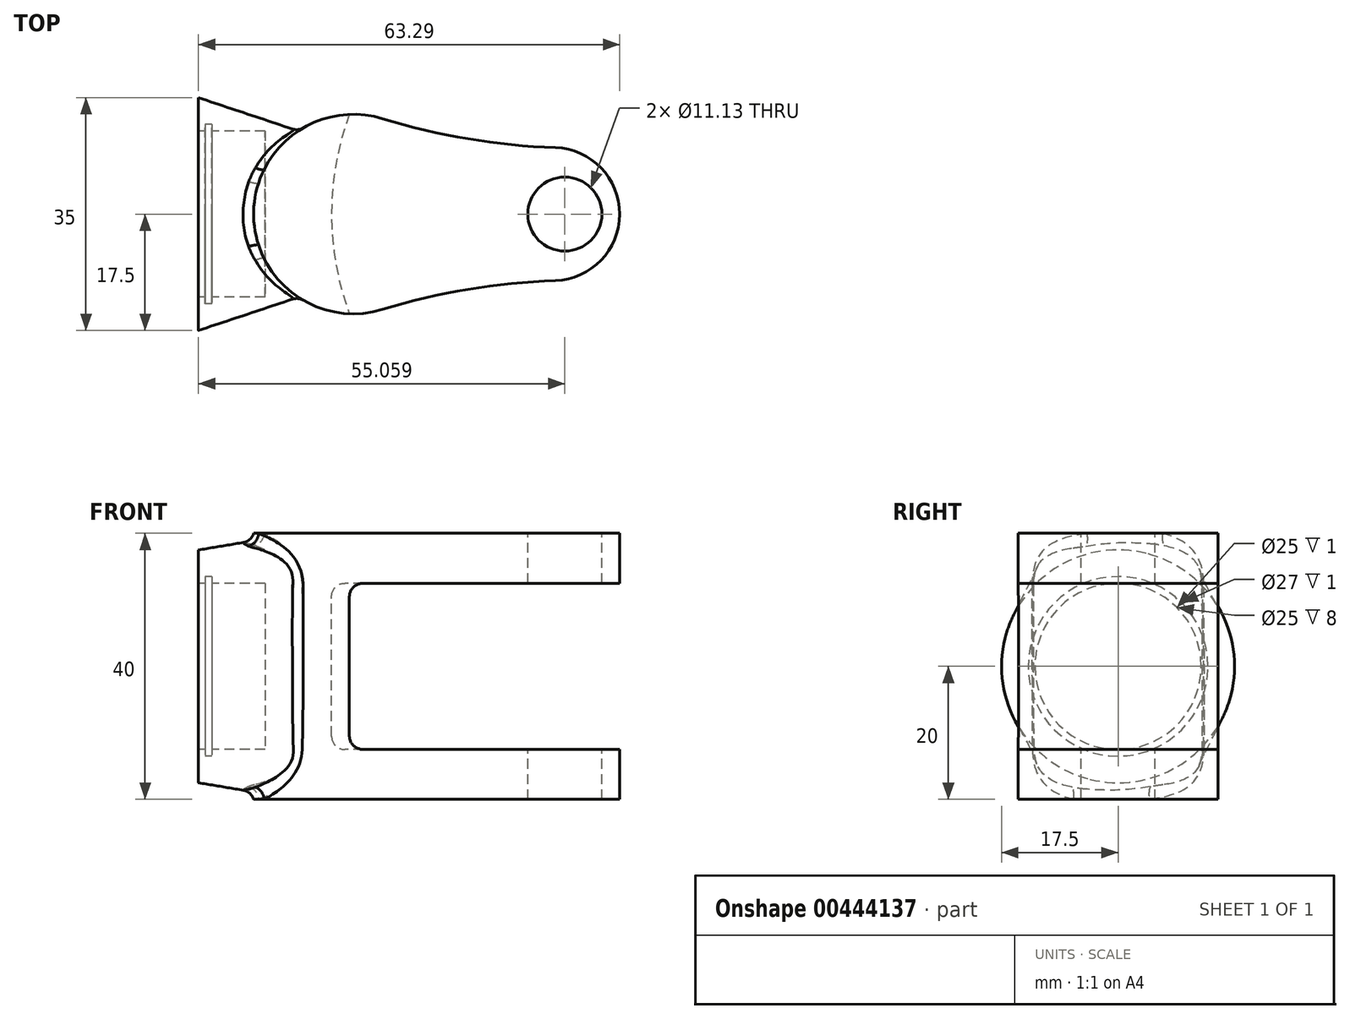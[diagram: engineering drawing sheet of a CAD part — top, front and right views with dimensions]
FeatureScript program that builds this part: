
annotation { "Feature Type Name" : "Feature", "Feature Type Description" : "" }
export const myFeature = defineFeature(function(context is Context, id is Id, definition is map)
    precondition{}
    {
        {
            var Q0;
            Q0=qCreatedBy(makeId("Right.planeOp"),FACE);
            var sketch = newSketch(context, id + "F0", { "sketchPlane" : qUnion([Q0])});
            skCircle(sketch, "E0", {"center": v(0, 0) * mm, "radius": 17.5 * mm});
            skSolve(sketch);
        }
        {
            var Q0;
            Q0=qCreatedBy(makeId("Right.planeOp"),FACE);
            cPlane(context, id + "F1", {"entities" : qUnion([Q0]), "cplaneType" : CPlaneType.OFFSET, "offset" : 15 * mm, "width" : 150 * mm, "height" : 150 * mm});
        }
        {
            var Q0;
            Q0=qCreatedBy(id+"F1.planeOp",FACE);
            var sketch = newSketch(context, id + "F2", { "sketchPlane" : qUnion([Q0])});
            skLineSegment(sketch, "E1.bottom", {"start": v(5, 20) * mm, "end": v(-5, 20) * mm});
            skLineSegment(sketch, "E1.top", {"start": v(5, -20) * mm, "end": v(-5, -20) * mm});
            skLineSegment(sketch, "E1.left", {"start": v(12.5, 12.5) * mm, "end": v(12.5, -12.5) * mm});
            skLineSegment(sketch, "E1.right", {"start": v(-12.5, 12.5) * mm, "end": v(-12.5, -12.5) * mm});
            skPoint(sketch, "E1.middle", {"position": v(0, 0) * mm});
            skPoint(sketch, "E2.visualSharp", {"position": v(-12.5, 20) * mm});
            skArc(sketch, "E2.filletArc", {"start": v(-5, 20) * mm, "mid": v(-10.3, 17.8) * mm, "end": v(-12.5, 12.5) * mm});
            skPoint(sketch, "E3.visualSharp", {"position": v(12.5, 20) * mm});
            skArc(sketch, "E3.filletArc", {"start": v(12.5, 12.5) * mm, "mid": v(10.3, 17.8) * mm, "end": v(5, 20) * mm});
            skPoint(sketch, "E4.visualSharp", {"position": v(12.5, -20) * mm});
            skArc(sketch, "E4.filletArc", {"start": v(5, -20) * mm, "mid": v(10.3, -17.8) * mm, "end": v(12.5, -12.5) * mm});
            skPoint(sketch, "E5.visualSharp", {"position": v(-12.5, -20) * mm});
            skArc(sketch, "E5.filletArc", {"start": v(-12.5, -12.5) * mm, "mid": v(-10.3, -17.8) * mm, "end": v(-5, -20) * mm});
            skSolve(sketch);
        }
        {
            var Q0;
            Q0=makeQuery(id+"F0.imprint","IMPRINT",FACE,{"disambiguationData":[TD([[makeQuery(id+"F0.imprint","IMPRINT",EDGE,{"derivedFrom":sQuery(id+"F0.wireOp",EDGE,"E0")}),1.0]])]});
            var Q1;
            Q1=makeQuery(id+"F2.imprint","IMPRINT",FACE,{"disambiguationData":[TD([[makeQuery(id+"F2.imprint","IMPRINT",EDGE,{"derivedFrom":sQuery(id+"F2.wireOp",EDGE,"E1.bottom")}),1.0]])]});
            loft(context, id + "F3", {"sheetProfilesArray" : [{ "sheetProfileEntities" : qUnion([Q0]) }, { "sheetProfileEntities" : qUnion([Q1]) }]});
        }
        {
            var Q0;
            Q0=qCreatedBy(makeId("Top.planeOp"),FACE);
            var sketch = newSketch(context, id + "F4", { "sketchPlane" : qUnion([Q0])});
            skArc(sketch, "E6", {"start": v(27.7, 14.34) * mm, "mid": v(8.3, 0) * mm, "end": v(27.7, -14.34) * mm});
            skArc(sketch, "E7", {"start": v(53.63, -10) * mm, "mid": v(63.3, 0) * mm, "end": v(53.63, 10) * mm});
            skArc(sketch, "E8", {"start": v(27.7, 14.34) * mm, "mid": v(40.52, 11.31) * mm, "end": v(53.63, 10) * mm});
            skArc(sketch, "E9", {"start": v(53.63, -10) * mm, "mid": v(40.52, -11.31) * mm, "end": v(27.7, -14.34) * mm});
            skSolve(sketch);
        }
        {
            var Q0;
            Q0 = qSketchRegion(id + "F4", true);
            extrude(context, id + "F5", {"entities" : qUnion([Q0]), "operationType" : NewBodyOperationType.ADD, "endBound" : BoundingType.SYMMETRIC, "depth" : 40 * mm});
        }
        {
            var Q0;
            Q0=qCreatedBy(makeId("Front.planeOp"),FACE);
            var sketch = newSketch(context, id + "F6", { "sketchPlane" : qUnion([Q0])});
            skLineSegment(sketch, "E10.bottom", {"start": v(63.3, -12.5) * mm, "end": v(20, -12.5) * mm});
            skLineSegment(sketch, "E10.top", {"start": v(63.3, 12.5) * mm, "end": v(20, 12.5) * mm});
            skLineSegment(sketch, "E10.left", {"start": v(63.3, -12.5) * mm, "end": v(63.3, 12.5) * mm});
            skLineSegment(sketch, "E10.right", {"start": v(20, -12.5) * mm, "end": v(20, 12.5) * mm});
            skPoint(sketch, "E10.middle", {"position": v(41.65, 0) * mm});
            skSolve(sketch);
        }
        {
            var Q0;
            Q0 = qSketchRegion(id + "F6", true);
            var Q1;
            Q1=sQuery(id+"F6.wireOp",EDGE,"E10.left");
            revolve(context, id + "F7", {"operationType" : NewBodyOperationType.REMOVE, "entities" : qUnion([Q0]), "axis" : qUnion([Q1]), "revolveType" : RevolveType.FULL, "oppositeDirection" : true});
        }
        {
            var Q0;
            Q0=makeQuery(id+"F3.opLoft","CAP_FACE",FACE,{"disambiguationData":[OSD([makeQuery(id+"F0.imprint","IMPRINT",FACE,{"disambiguationData":[TD([[makeQuery(id+"F0.imprint","IMPRINT",EDGE,{"derivedFrom":sQuery(id+"F0.wireOp",EDGE,"E0")}),1.0]])]})])],"isStart":true});
            var sketch = newSketch(context, id + "F8", { "sketchPlane" : qUnion([Q0])});
            skCircle(sketch, "E11", {"center": v(0, 0) * mm, "radius": 12.5 * mm});
            skSolve(sketch);
        }
        {
            var Q0;
            Q0 = qSketchRegion(id + "F8", true);
            extrude(context, id + "F9", {"entities" : qUnion([Q0]), "operationType" : NewBodyOperationType.REMOVE, "oppositeDirection" : true, "depth" : 10 * mm});
        }
        {
            var Q0;
            Q0=makeQuery(id+"F3.opLoft","CAP_FACE",FACE,{"disambiguationData":[OSD([makeQuery(id+"F0.imprint","IMPRINT",FACE,{"disambiguationData":[TD([[makeQuery(id+"F0.imprint","IMPRINT",EDGE,{"derivedFrom":sQuery(id+"F0.wireOp",EDGE,"E0")}),1.0]])]})])],"isStart":true});
            cPlane(context, id + "F10", {"entities" : qUnion([Q0]), "cplaneType" : CPlaneType.OFFSET, "offset" : 1 * mm, "oppositeDirection" : true, "width" : 150 * mm, "height" : 150 * mm});
        }
        {
            var Q0;
            Q0=qCreatedBy(id+"F10.planeOp",FACE);
            var sketch = newSketch(context, id + "F11", { "sketchPlane" : qUnion([Q0])});
            skCircle(sketch, "E12.0", {"center": v(0, 0) * mm, "radius": 13.5 * mm});
            skSolve(sketch);
        }
        {
            var Q0;
            Q0 = qSketchRegion(id + "F11", true);
            extrude(context, id + "F12", {"entities" : qUnion([Q0]), "operationType" : NewBodyOperationType.REMOVE, "oppositeDirection" : true, "depth" : 1 * mm});
        }
        {
            var Q0;
            Q0=makeQuery(id+"F5.opExtrude","CAP_FACE",FACE,{"disambiguationData":[OSD([sQuery(id+"F4.wireOp",EDGE,"E6"),sQuery(id+"F4.wireOp",EDGE,"E7"),sQuery(id+"F4.wireOp",EDGE,"E8"),sQuery(id+"F4.wireOp",EDGE,"E9")])],"isStart":false});
            var sketch = newSketch(context, id + "F13", { "sketchPlane" : qUnion([Q0])});
            skCircle(sketch, "E13", {"center": v(55.06, 0) * mm, "radius": 5.57 * mm});
            skSolve(sketch);
        }
        {
            var Q0;
            Q0 = qSketchRegion(id + "F13", true);
            extrude(context, id + "F14", {"entities" : qUnion([Q0]), "operationType" : NewBodyOperationType.REMOVE, "endBound" : BoundingType.THROUGH_ALL, "oppositeDirection" : true, "depth" : 25 * mm});
        }
        {
            var Q0;
            Q0=makeQuery(id+"F7.boolean.opBoolean","COPY",EDGE,{"derivedFrom":makeQuery(id+"F7.opRevolve","SWEPT_EDGE",EDGE,{"disambiguationData":[OSD([sQuery(id+"F6.wireOp",EDGE,"E10.bottom"),sQuery(id+"F6.wireOp",EDGE,"E10.right")])]})});
            var Q1;
            Q1=makeQuery(id+"F7.boolean.opBoolean","COPY",EDGE,{"derivedFrom":makeQuery(id+"F7.opRevolve","SWEPT_EDGE",EDGE,{"disambiguationData":[OSD([sQuery(id+"F6.wireOp",EDGE,"E10.top"),sQuery(id+"F6.wireOp",EDGE,"E10.right")])]})});
            var Q2;
            Q2=makeQuery(id+"F5.boolean.opBoolean","INTERSECT",EDGE,{"disambiguationData":[OD(1.0)],"derivedFrom":[makeQuery(id+"F3.opLoft","SWEPT_FACE",FACE,{"disambiguationData":[OSD([sQuery(id+"F0.wireOp",EDGE,"E0"),sQuery(id+"F2.wireOp",EDGE,"E1.bottom"),sQuery(id+"F2.wireOp",EDGE,"E2.filletArc"),sQuery(id+"F2.wireOp",EDGE,"E3.filletArc")])]}),makeQuery(id+"F5.opExtrude","SWEPT_FACE",FACE,{"disambiguationData":[OSD([sQuery(id+"F4.wireOp",EDGE,"E6")])]})]});
            fillet(context, id + "F15", {"entities" : qUnion([Q0, Q1, Q2]), "radius" : 2 * mm, "tangentPropagation" : true, "allowEdgeOverflow" : false});
        }
    });
